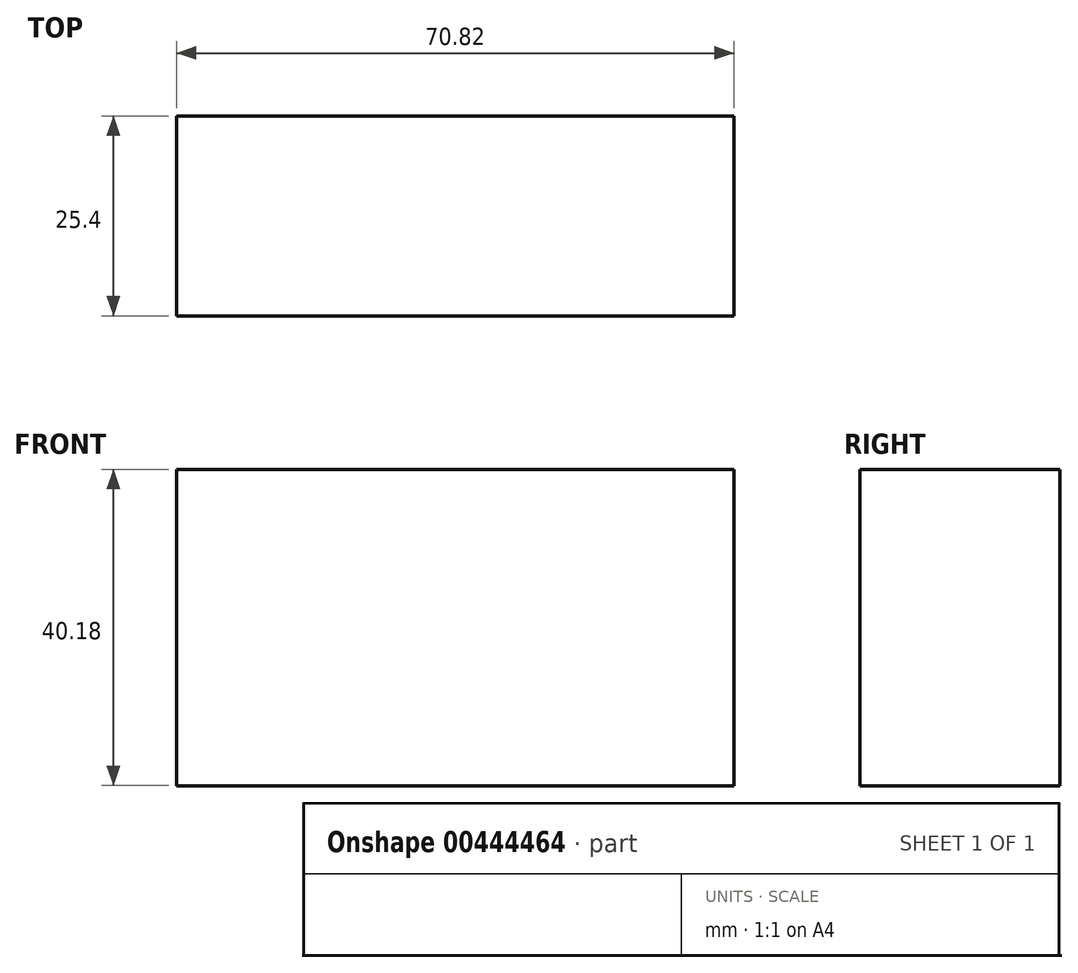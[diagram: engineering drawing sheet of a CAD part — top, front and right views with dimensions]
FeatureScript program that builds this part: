
annotation { "Feature Type Name" : "Feature", "Feature Type Description" : "" }
export const myFeature = defineFeature(function(context is Context, id is Id, definition is map)
    precondition{}
    {
        {
            var Q0;
            Q0=qCreatedBy(makeId("Front.planeOp"),FACE);
            var sketch = newSketch(context, id + "F0", { "sketchPlane" : qUnion([Q0])});
            skLineSegment(sketch, "E0.bottom", {"start": v(-1.18, 33.88) * mm, "end": v(69.64, 33.88) * mm});
            skLineSegment(sketch, "E0.top", {"start": v(-1.18, -6.3) * mm, "end": v(69.64, -6.3) * mm});
            skLineSegment(sketch, "E0.left", {"start": v(-1.18, 33.88) * mm, "end": v(-1.18, -6.3) * mm});
            skLineSegment(sketch, "E0.right", {"start": v(69.64, 33.88) * mm, "end": v(69.64, -6.3) * mm});
            skCircle(sketch, "E1", {"center": v(8.68, 3.95) * mm, "radius": 3.42 * mm});
            skCircle(sketch, "E2", {"center": v(59.95, 0) * mm, "radius": 3.74 * mm});
            skCircle(sketch, "E3", {"center": v(7.65, 21.5) * mm, "radius": 3.28 * mm});
            skCircle(sketch, "E4", {"center": v(58.86, 22.18) * mm, "radius": 4.08 * mm});
            skSolve(sketch);
        }
        {
            var Q0;
            Q0=makeQuery(id+"F0.imprint","IMPRINT",FACE,{"disambiguationData":[TD([[makeQuery(id+"F0.imprint","IMPRINT",EDGE,{"derivedFrom":sQuery(id+"F0.wireOp",EDGE,"E4")}),1.0]])]});
            var Q1;
            Q1=makeQuery(id+"F0.imprint","IMPRINT",FACE,{"disambiguationData":[TD([[makeQuery(id+"F0.imprint","IMPRINT",EDGE,{"derivedFrom":sQuery(id+"F0.wireOp",EDGE,"E2")}),1.0]])]});
            var Q2;
            Q2=makeQuery(id+"F0.imprint","IMPRINT",FACE,{"disambiguationData":[TD([[makeQuery(id+"F0.imprint","IMPRINT",EDGE,{"derivedFrom":sQuery(id+"F0.wireOp",EDGE,"E1")}),1.0]])]});
            var Q3;
            Q3=makeQuery(id+"F0.imprint","IMPRINT",FACE,{"disambiguationData":[TD([[makeQuery(id+"F0.imprint","IMPRINT",EDGE,{"derivedFrom":sQuery(id+"F0.wireOp",EDGE,"E3")}),1.0]])]});
            var Q4;
            Q4=makeQuery(id+"F0.imprint","IMPRINT",FACE,{"disambiguationData":[TD([[makeQuery(id+"F0.imprint","IMPRINT",EDGE,{"derivedFrom":sQuery(id+"F0.wireOp",EDGE,"E0.bottom")}),-1.0]])]});
            extrude(context, id + "F1", {"entities" : qUnion([Q0, Q1, Q2, Q3, Q4]), "depth" : 25.4 * mm});
        }
    });
